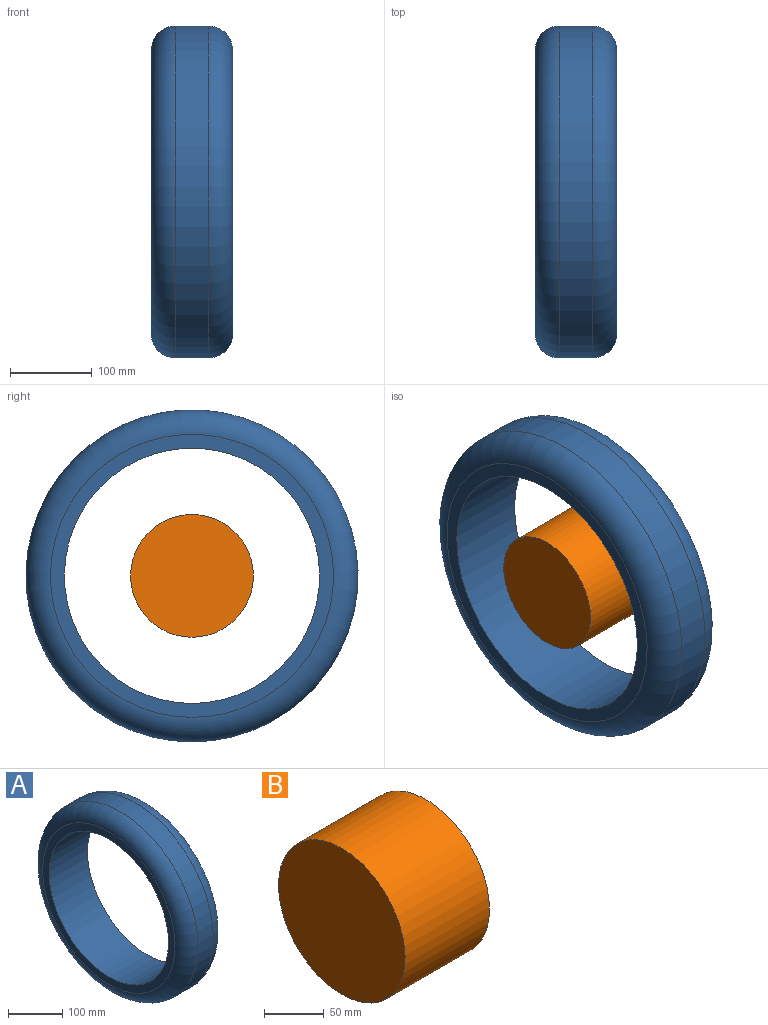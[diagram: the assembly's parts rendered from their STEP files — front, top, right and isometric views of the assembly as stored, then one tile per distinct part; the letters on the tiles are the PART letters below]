
ASSEMBLY  parts=2 mates=1
PART A: 6 faces, bbox 100x439.5x439.5 mm
  f0: cylinder r=203mm len=406mm, axis (-1,0,0), area 51019.5mm2, adj f4,f5
  f1: plane 346x346mm, normal (1,0,0), area 17570.9mm2, adj f2,f4
  f2: cylinder r=156mm len=312mm, axis (-1,0,0), area 98017.7mm2, adj f1,f3
  f3: plane 346x346mm, normal (-1,0,0), area 17570.9mm2, adj f2,f5
  f4: torus R=173mm, axis (1,0,0), area 56878.1mm2, adj f0,f1
  f5: torus R=173mm, axis (1,0,0), area 56878.1mm2, adj f0,f3
PART B: 3 faces, bbox 100x150x150 mm
  f0: plane 150x150mm, normal (-1,0,0), area 17671.5mm2, adj f1
  f1: cylinder r=75mm len=150mm, axis (-1,0,0), area 47123.9mm2, adj f0,f2
  f2: plane 150x150mm, normal (1,0,0), area 17671.5mm2, adj f1
PLACE A t=(22.31,-2499.57,-417.18)mm
PLACE B t=(-837.69,-2499.57,-417.18)mm
MATE revolute A.f4 <-> B.f1  axis (-1,0,0) through (122.31,-202.57,-214.18)mm
